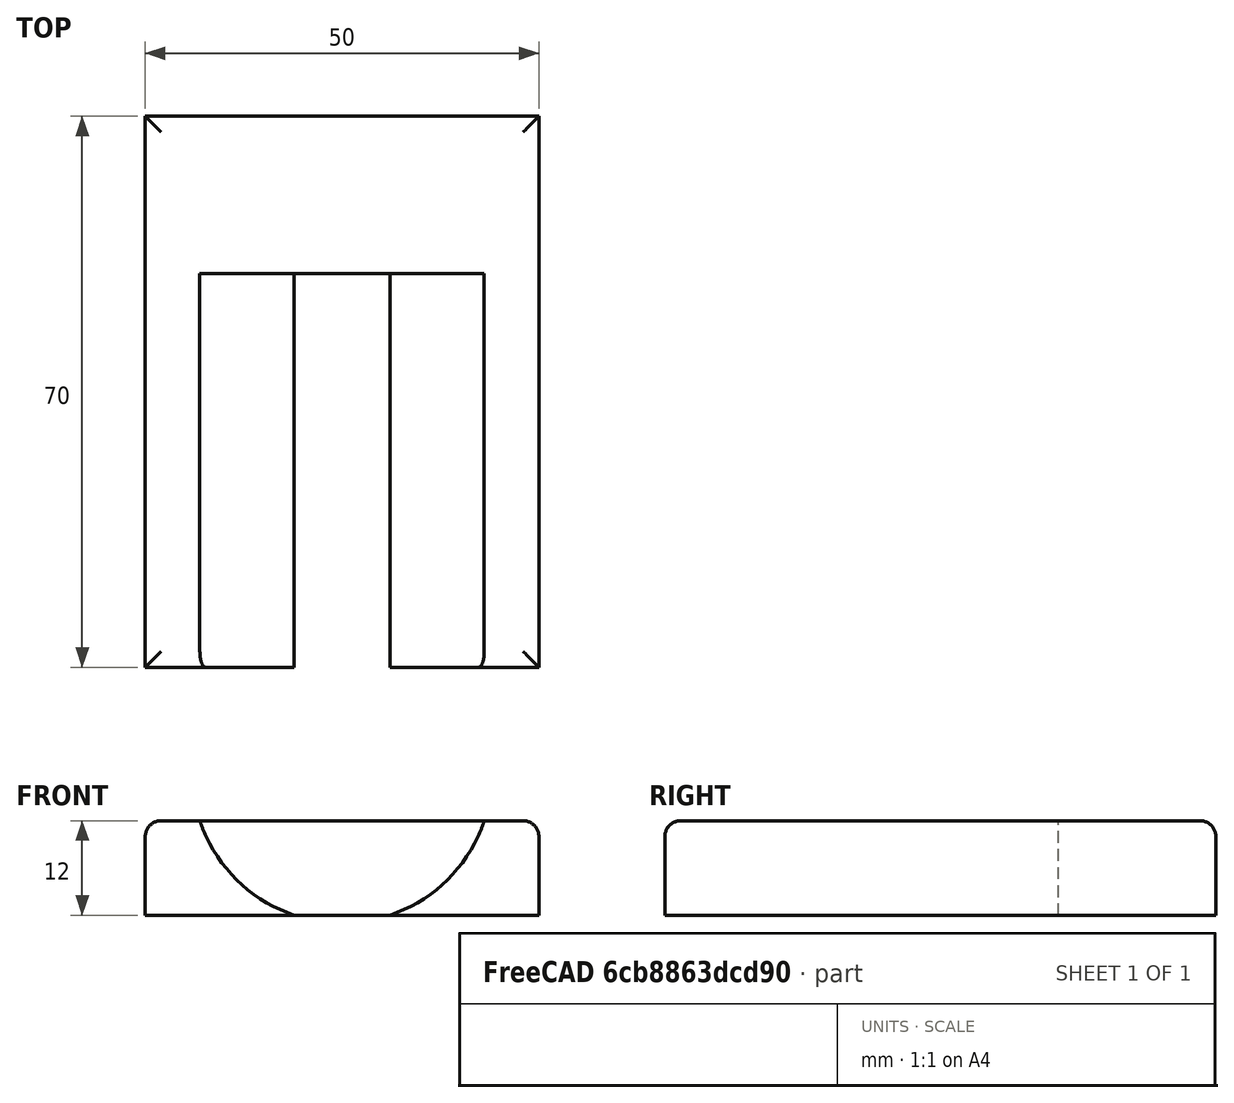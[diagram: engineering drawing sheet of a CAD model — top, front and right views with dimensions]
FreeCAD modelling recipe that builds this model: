
FCSTD DOCUMENT  (FreeCAD 0.21R33771 (Git))
Label: FridgeWheelChock
License: All rights reserved
LicenseURL: http://en.wikipedia.org/wiki/All_rights_reserved
objects: Sketcher::SketchObject×2, Spreadsheet::Sheet×1, PartDesign::Pad×1, PartDesign::Pocket×1, PartDesign::Fillet×1, PartDesign::Body×1, App::Part×1, Mesh::Feature×1
note: 9 computed .brp shape members not serialized (recipe doc carries the construction recipe); baked Part::Feature solids carry a one-line shape summary decoded from their .brp

FEATURE [Spreadsheet::Sheet] Spreadsheet  label="Parameters"
  cells = A2='Wheel; B3='Diameter; C3=1.5; D3='inches; C4(wheel_diameter)==C3 * 25.4; D4='mm; B6='Length; C6=1; D6='inches; C7(wheel_length)==C6 * 25.4; D7='mm; A9='Chock; B10='Height; C10(height)=12; D10='mm; B11='Length; C11(length)=70; D11='mm; B12='Width; C12(width)=50; D12='mm; B13='Center Offset; C13(offset_center)=15; D13='mm; B14='Height 'Offset; C14(offset_height)=1; D14='mm
FEATURE [Sketcher::SketchObject] Sketch  label="Base-Sketch"
  FullyConstrained = true
  MapMode = 5
  Support = -> [XY_Plane001]
  expr: Constraints[10] = <<Parameters>>.length / 2 - <<Parameters>>.offset_center
  expr: Constraints[7] = <<Parameters>>.width
  expr: Constraints[8] = <<Parameters>>.length
  sketch-geometry (4):
    g0: LineSegment StartX=-25 StartY=20 StartZ=0 EndX=25 EndY=20 EndZ=0
    g1: LineSegment StartX=25 StartY=20 StartZ=0 EndX=25 EndY=-50 EndZ=0
    g2: LineSegment StartX=25 StartY=-50 StartZ=0 EndX=-25 EndY=-50 EndZ=0
    g3: LineSegment StartX=-25 StartY=-50 StartZ=0 EndX=-25 EndY=20 EndZ=0
  constraints (11):
    c: Coincident(g0,g1)
    c: Coincident(g1,g2)
    c: Coincident(g2,g3)
    c: Coincident(g3,g0)
    c: Horizontal(g2)
    c: Vertical(g1)
    c: Vertical(g3)
    c: DistanceX(g0,g0) = 50
    c: DistanceY(g1,g1) = 70
    c: Symmetric(g0,g0,g-2)
    c: DistanceY(g-1,g0) = 20
FEATURE [PartDesign::Pad] Pad
  Direction = (0,0,1)
  Length = 12
  Length2 = 10
  Profile = -> Sketch
  ReferenceAxis = -> Sketch [N_Axis]
  Type = 0
  expr: Length = <<Parameters>>.height
FEATURE [Sketcher::SketchObject] Sketch001  label="Pocket-Sketch"
  FullyConstrained = true
  MapMode = 5
  Placement = pos=(0,0,0) rot=(1,0,0;1.5708rad)
  Support = -> [XZ_Plane001]
  expr: Constraints[1] = <<Parameters>>.wheel_diameter
  expr: Constraints[2] = <<Parameters>>.wheel_diameter / 2 - <<Parameters>>.offset_height
  sketch-geometry (1):
    g0: Circle CenterX=0 CenterY=18.05 CenterZ=0 NormalX=0 NormalY=0 NormalZ=1 AngleXU=0 Radius=19.05
  constraints (3):
    c: PointOnObject(g0,g-2)
    c: Diameter(g0) = 38.1
    c: DistanceY(g-1,g0) = 18.05
FEATURE [PartDesign::Pocket] Pocket
  BaseFeature = -> Pad
  Direction = (0,1,2e-16)
  Length = 71
  Length2 = 5
  Profile = -> Sketch001
  ReferenceAxis = -> Sketch001 [N_Axis]
  Reversed = true
  Type = 0
  expr: Length = <<Parameters>>.length + 1
FEATURE [PartDesign::Fillet] Fillet
  Base = -> Pocket [Edge7,Edge4,Edge10,Edge16,Edge20]
  BaseFeature = -> Pocket
  Radius = 2
  SupportTransform = false
  UseAllEdges = false
FEATURE [PartDesign::Body] Body
  Group = -> [Sketch,Pad,Sketch001,Pocket,Fillet]
  Origin = -> Origin001
  Tip = -> Fillet
FEATURE [App::Part] Part
  Group = -> [Body]
  Origin = -> Origin
FEATURE [Mesh::Feature] Mesh  label="Fillet (Meshed)"
